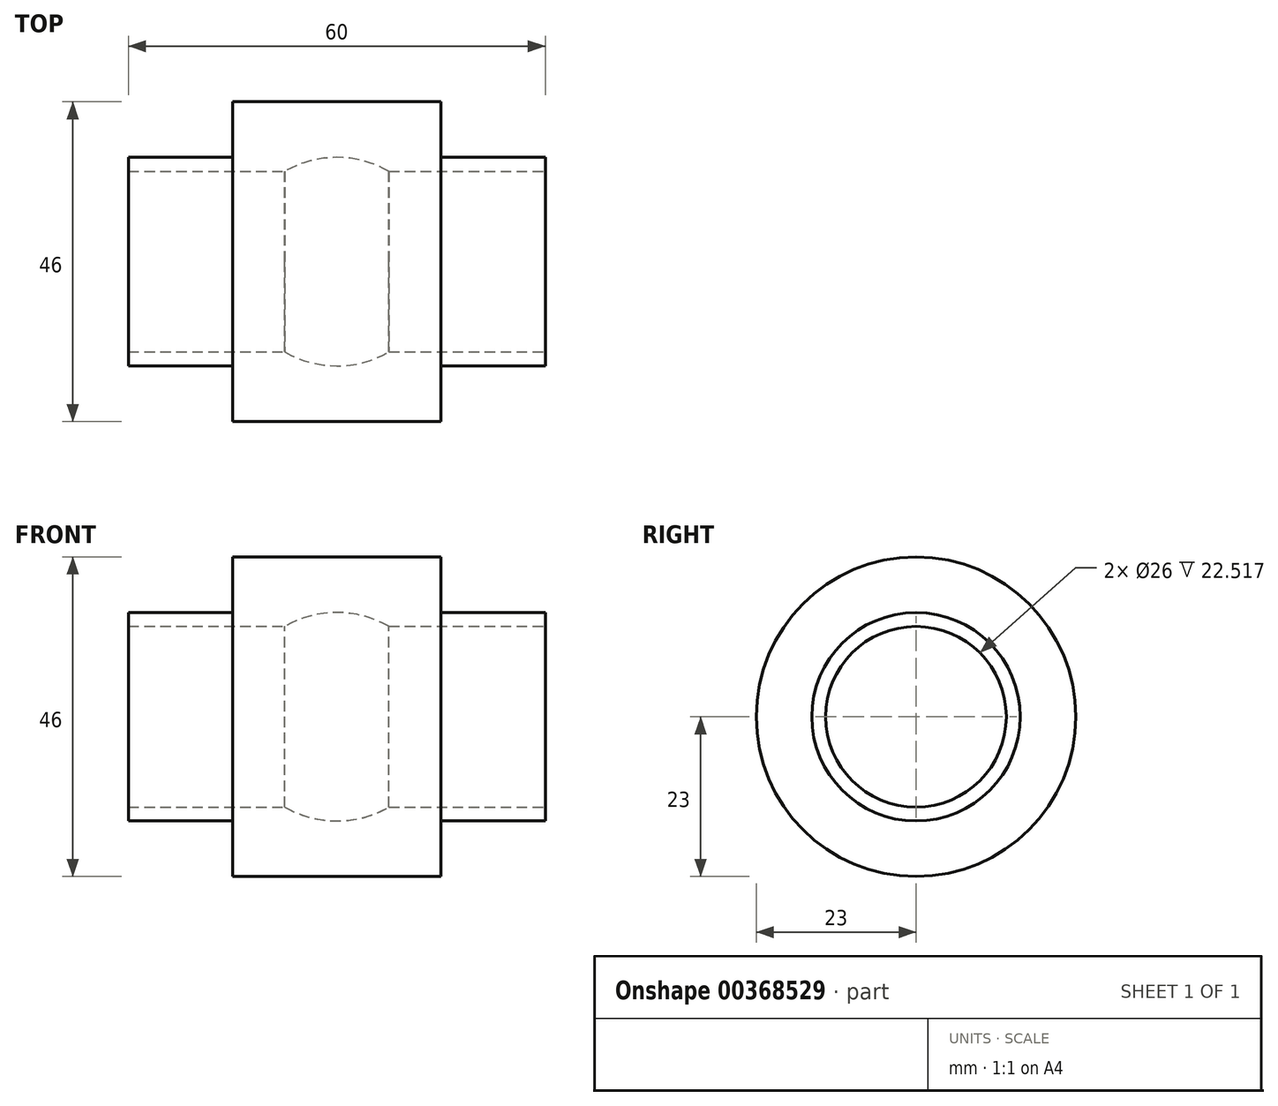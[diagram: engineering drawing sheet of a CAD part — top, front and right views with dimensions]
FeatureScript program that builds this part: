
annotation { "Feature Type Name" : "Feature", "Feature Type Description" : "" }
export const myFeature = defineFeature(function(context is Context, id is Id, definition is map)
    precondition{}
    {
        {
            var Q0;
            Q0=qCreatedBy(makeId("Front.planeOp"),FACE);
            var sketch = newSketch(context, id + "F0", { "sketchPlane" : qUnion([Q0])});
            skLineSegment(sketch, "E0", {"start": v(-7.48, 13) * mm, "end": v(-30, 13) * mm});
            skLineSegment(sketch, "E1", {"start": v(-30, 13) * mm, "end": v(-30, 15) * mm});
            skLineSegment(sketch, "E2", {"start": v(-30, 15) * mm, "end": v(-15, 15) * mm});
            skLineSegment(sketch, "E3", {"start": v(-15, 15) * mm, "end": v(-15, 23) * mm});
            skLineSegment(sketch, "E4", {"start": v(-15, 23) * mm, "end": v(15, 23) * mm});
            skLineSegment(sketch, "E5", {"start": v(15, 23) * mm, "end": v(15, 15) * mm});
            skLineSegment(sketch, "E6", {"start": v(15, 15) * mm, "end": v(30, 15) * mm});
            skLineSegment(sketch, "E7", {"start": v(30, 15) * mm, "end": v(30, 13) * mm});
            skLineSegment(sketch, "E8", {"start": v(30, 13) * mm, "end": v(7.48, 13) * mm});
            skArc(sketch, "E9", {"start": v(7.48, 13) * mm, "mid": v(0, 15) * mm, "end": v(-7.48, 13) * mm});
            skLineSegment(sketch, "E10", {"start": v(0, 0) * mm, "end": v(-53.07, 0) * mm, "construction": true});
            skSolve(sketch);
        }
        {
            var Q0;
            Q0 = qSketchRegion(id + "F0", true);
            var Q1;
            Q1=sQuery(id+"F0.wireOp",EDGE,"E10");
            revolve(context, id + "F1", {"entities" : qUnion([Q0]), "axis" : qUnion([Q1]), "revolveType" : RevolveType.FULL});
        }
    });
